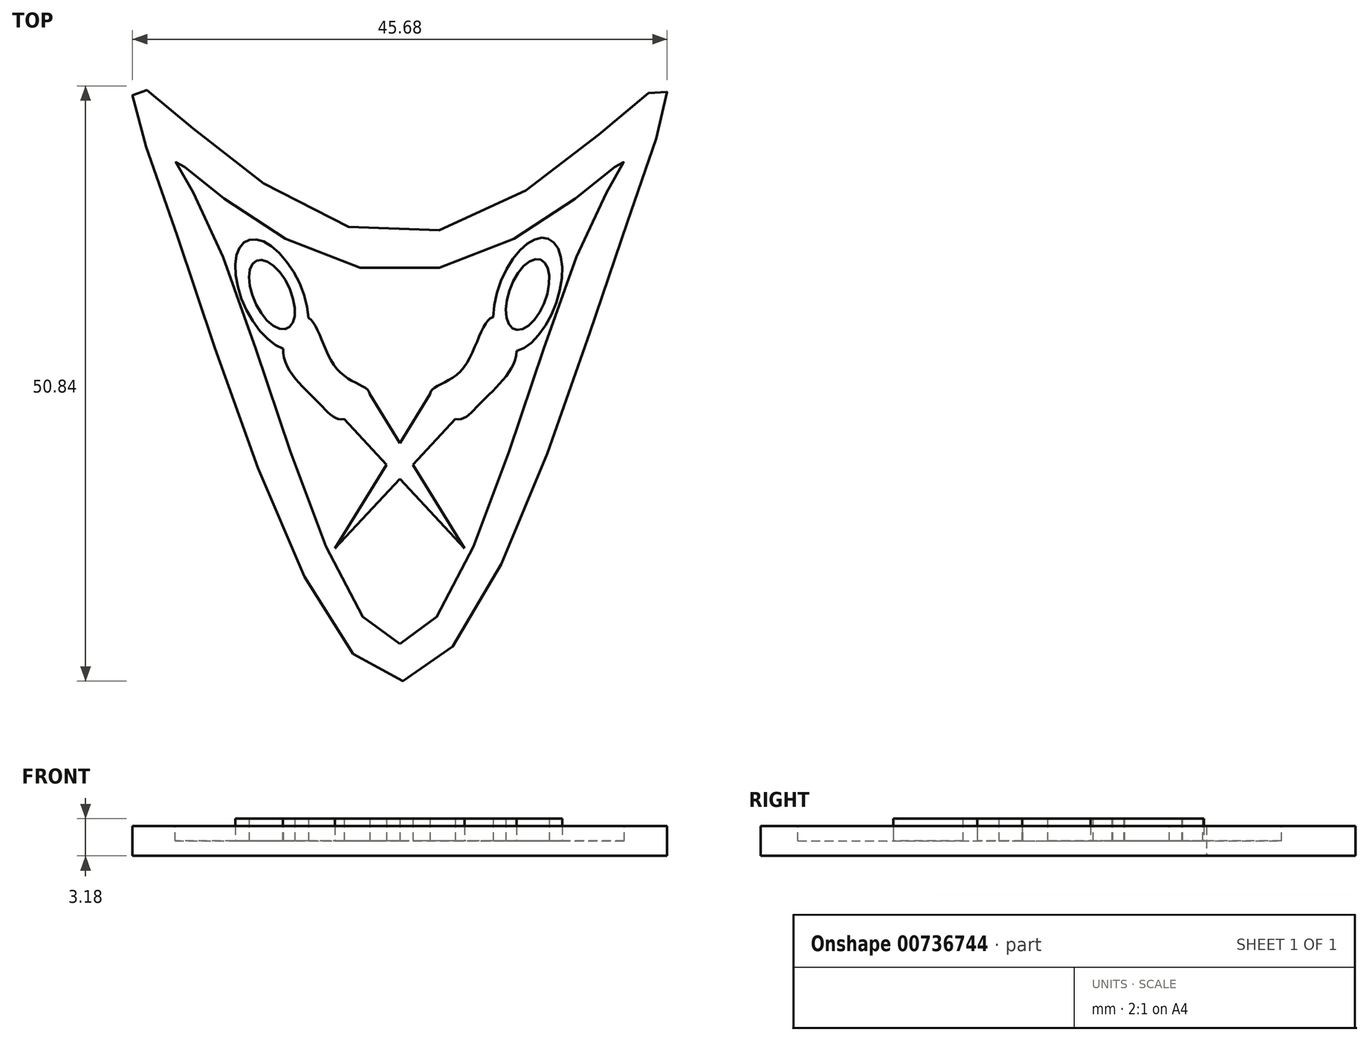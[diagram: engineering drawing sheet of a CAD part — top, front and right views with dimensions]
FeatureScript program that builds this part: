
annotation { "Feature Type Name" : "Feature", "Feature Type Description" : "" }
export const myFeature = defineFeature(function(context is Context, id is Id, definition is map)
    precondition{}
    {
        {
            var Q0;
            Q0=qCreatedBy(makeId("Top.planeOp"),FACE);
            var sketch = newSketch(context, id + "F0", { "sketchPlane" : qUnion([Q0])});
            skFitSpline(sketch, "E0", {"points": [v(-19.05, 0) * mm, v(0, -38.1) * mm, v(19.05, 0) * mm, v(22.23, 12.7) * mm, v(0, 0) * mm, v(-22.23, 12.7) * mm, v(-19.05, 0) * mm]});
            skSolve(sketch);
        }
        {
            var Q0;
            Q0 = qSketchRegion(id + "F0", true);
            extrude(context, id + "F1", {"entities" : qUnion([Q0]), "depth" : 2.54 * mm, "offsetDistance" : 25.4 * mm});
        }
        {
            var Q0;
            Q0=makeQuery(id+"F1.opExtrude","CAP_FACE",FACE,{"disambiguationData":[OSD([sQuery(id+"F0.wireOp",EDGE,"E0")])],"isStart":false});
            var sketch = newSketch(context, id + "F2", { "sketchPlane" : qUnion([Q0])});
            skFitSpline(sketch, "E1", {"points": [v(0, -34.93) * mm, v(15.88, 0) * mm, v(19.05, 6.35) * mm, v(0, -3.18) * mm, v(-19.05, 6.35) * mm, v(-15.88, 0) * mm, v(0, -34.93) * mm]});
            skSolve(sketch);
        }
        {
            var Q0;
            Q0 = qSketchRegion(id + "F2", true);
            extrude(context, id + "F3", {"entities" : qUnion([Q0]), "operationType" : NewBodyOperationType.REMOVE, "oppositeDirection" : true, "depth" : 1.27 * mm, "offsetDistance" : 25.4 * mm});
        }
        {
            var Q0;
            Q0=makeQuery(id+"F3.boolean.opBoolean","COPY",FACE,{"derivedFrom":makeQuery(id+"F3.opExtrude","CAP_FACE",FACE,{"disambiguationData":[OSD([sQuery(id+"F2.wireOp",EDGE,"E1")])],"isStart":false})});
            var sketch = newSketch(context, id + "F4", { "sketchPlane" : qUnion([Q0])});
            skEllipse(sketch, "E2", {"center": v(-10.92, -5.08) * mm, "majorRadius": 5.08 * mm, "minorRadius": 2.54 * mm, "majorAxis": v(-0.42, 0.9)});
            skEllipse(sketch, "E3", {"center": v(-10.92, -5.08) * mm, "majorRadius": 3.18 * mm, "minorRadius": 1.59 * mm, "majorAxis": v(-0.42, 0.9)});
            skEllipse(sketch, "E4.2.0.0", {"center": v(10.92, -5.08) * mm, "majorRadius": 5.08 * mm, "minorRadius": 2.54 * mm, "majorAxis": v(0.34, 0.94)});
            skEllipse(sketch, "E4.2.0.1", {"center": v(10.92, -5.08) * mm, "majorRadius": 3.18 * mm, "minorRadius": 1.59 * mm, "majorAxis": v(0.35, 0.94)});
            skLineSegment(sketch, "E4.direction1", {"start": v(-10.92, -5.08) * mm, "end": v(0, -5.08) * mm, "construction": true});
            skLineSegment(sketch, "E4.direction2", {"start": v(-10.92, -5.08) * mm, "end": v(-10.92, 20.57) * mm, "construction": true});
            skFitSpline(sketch, "E5", {"points": [v(7.97, -7) * mm, v(5.23, -11.6) * mm, v(2.58, -13.57) * mm, v(4.76, -15.7) * mm, v(6.88, -14.36) * mm, v(9.98, -9.85) * mm, v(7.97, -7) * mm]});
            skLineSegment(sketch, "E6", {"start": v(-4.76, -15.7) * mm, "end": v(5.54, -26.77) * mm});
            skLineSegment(sketch, "E7", {"start": v(5.54, -26.77) * mm, "end": v(-2.58, -13.57) * mm});
            skFitSpline(sketch, "E8.MirrorC", {"points": [v(-7.97, -7) * mm, v(-5.23, -11.6) * mm, v(-2.58, -13.57) * mm, v(-4.76, -15.7) * mm, v(-6.88, -14.36) * mm, v(-9.98, -9.85) * mm, v(-7.97, -7) * mm]});
            skLineSegment(sketch, "E9.MirrorCS", {"start": v(-5.54, -26.77) * mm, "end": v(2.58, -13.57) * mm});
            skLineSegment(sketch, "E10.MirrorCS", {"start": v(4.76, -15.7) * mm, "end": v(-5.54, -26.77) * mm});
            skSolve(sketch);
        }
        {
            var Q0;
            Q0 = qSketchRegion(id + "F4", true);
            extrude(context, id + "F5", {"entities" : qUnion([Q0]), "operationType" : NewBodyOperationType.ADD, "depth" : 1.9 * mm, "offsetDistance" : 25.4 * mm});
        }
    });
